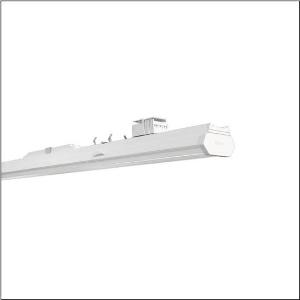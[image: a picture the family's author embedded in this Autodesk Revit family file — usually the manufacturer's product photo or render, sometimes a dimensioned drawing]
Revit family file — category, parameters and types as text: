
# Revit family: licross_r__21_protected_mo_52td117n485g_f66a
name_source: partatom
category: Lighting Fixtures
units: mm (PartAtom-declared; Revit-internal decimal feet)

## family parameters
Cut with Voids When Loaded = No
Host = Face
Light Source = No
Part Type = Normal
Room Calculation Point = No
Round Connector Dimension = Use Diameter
Shared = No

## types (1)
- Licross® 21 Protected MO (1 x LED, 8570 lm, 47.9 W, 4000K)
    Apparent Load = 48 VA
    CIE Flux Codes = 83 94 98 100 100
    Color Rendering = 80
    Color Temperature = 4000K
    Default Elevation = 1800 mm
    Description = Licross® 21 Protected MO, luminaire insert, of sheet steel, galvanised, coil coated, white, length: 1.500mm, width: 66mm, height: 67mm, LED rated luminous flux: 8.570lm, light colour: 840, control gear: ON/OFF, with plug, 3-pole, with phase selection, mains connection: 220..240V, AC, 50/60Hz, rated input power: 48W, halogen-free wiring, primary light control with lens, of plastic, primary optical cover: cover, of PMMA, light emission: direct distribution, primary light characteristic: symmetric, protection rating (complete): IP54, insulation class (complete): insulation class I (protective earthing), certification: CE, ENEC, VDE, UKCA, protection symbol: D if used in an environment with non-conductive dust loads with corresponding accessories, impact resistance: IK06, permissible ambient temperature for indoor applications: -35..+45°C, corresponds to IFS (International Featured Standards) requirements for safety and quality in the food industry, reducing of maximum allowable ambient temperature of 5°C with ceiling mounting, LABS conformity tested according to VDMA 24364:2018-05, packaging unit: 1 piece
    Height = 92 mm
    Lamp = 1 x LED
    Lamp Light Flux = 8570 lm
    Lamp Power = 47.9 W
    Lamp count = 1
    Length = 1500 mm
    Luminous efficacy = 179 lm/W
    Manufacturer = Siteco
    ModVariant = No
    Model = 52TD117N485G
    Mounting Place = Ceiling
    Mounting Type = Pendant
    Number of Poles = 1
    OnlyDefault = Yes
    Power Factor = 1
    Product Name = Licross® 21 Protected MO
    Product group = luminaire insert
    ProductGroupID = 901
    Protection Class = Protection class I
    Protection Degree = IP 54
    RLX_Detail_Level = 1
    RLX_Emergency_Light_Flux = 0 lm
    RLX_Emergency_Type = 0
    RLX_Emergency_Type_DB = No
    RlxData = <blob elided: 20385 chars, md5=675f6a0a>
    Socket = socket
    Standby Power = 0 W
    System Light Flux = 8570 lm
    System Power = 48 W
    Type Comments = Product without accessories
    Type Image = l_1256148.jpg
    URL = http://relux.com
    VarID = ---
    Voltage = 0 V
    Weight = 0.00 kg
    Width = 88 mm

## geometry (parser evidence)
native form markers: Blend x4, Sweep x10
no freeform markers — native parametric forms only
